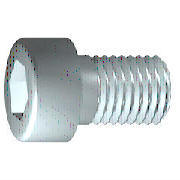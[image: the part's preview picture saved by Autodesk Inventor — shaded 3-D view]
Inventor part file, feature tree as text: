
AUTODESK INVENTOR PART (.ipt)
format: ipt  version: 2017 (Build 210142000, 142)  size: 193,024 bytes
history: native  units: mm (DEFAULTED — no unit token found)
features: sketch x2, extrude x1, plane x1, fillet x1
ambient origin geometry x7: Origin, YZ Plane, XY Plane, X Axis, Y Axis, Z Axis, Center Point
bodies: Solid1 (feature_tree), Body (feature_tree)
feature tree (5):
  extrude  "Slot"  Depth=5.0mm
  plane  "Work Plane1"
  fillet  "Fillet2"  Radius=5.0mm
  sketch  "Sketch1"  dims[d1=7.90924mm d2=0.49086mm d3=5.0mm]
  sketch  "Sketch2"  dims[d4=2.5mm d5=60.0deg d6=5.0mm d7=5.0mm d8=4.618802mm d9=8.5mm d10=90.0deg d11=10.0mm d12=0.0mm d13=7.90924mm d14=0.0mm d15=0.49076mm d16=0.49076mm d17=0.5mm d19=0.0mm d26=10.0mm d27=45.0deg d28=0.0mm d29=0.0mm d30=0.1mm]
